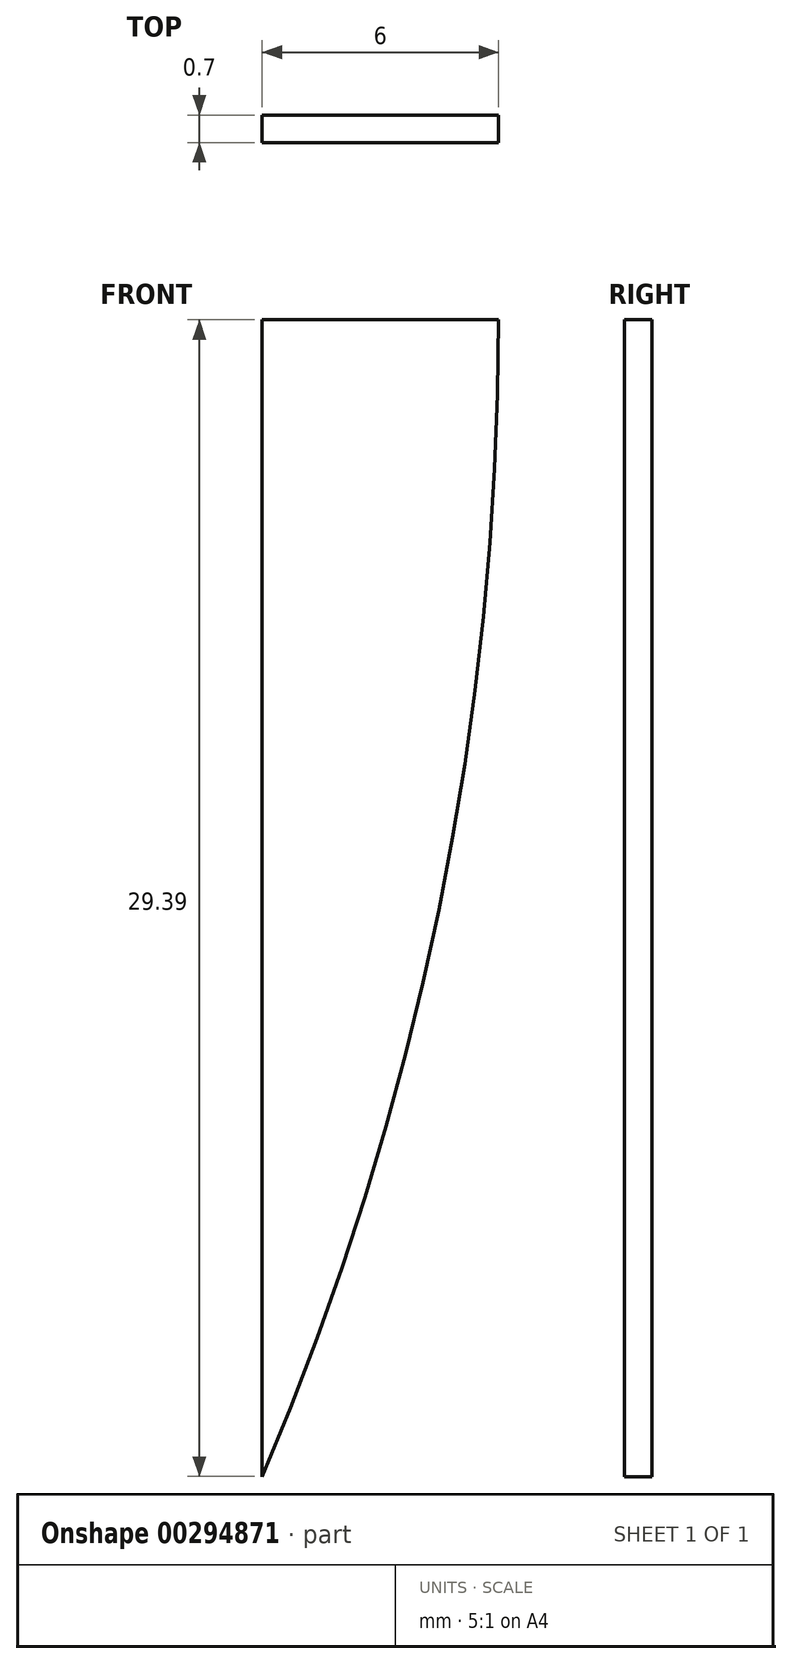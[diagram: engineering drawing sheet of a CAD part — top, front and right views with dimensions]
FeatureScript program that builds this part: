
annotation { "Feature Type Name" : "Feature", "Feature Type Description" : "" }
export const myFeature = defineFeature(function(context is Context, id is Id, definition is map)
    precondition{}
    {
        {
            var Q0;
            Q0=qCreatedBy(makeId("Front.planeOp"),FACE);
            var sketch = newSketch(context, id + "F0", { "sketchPlane" : qUnion([Q0])});
            skCircle(sketch, "E0", {"center": v(0, 0) * mm, "radius": 75 * mm});
            skLineSegment(sketch, "E1", {"start": v(69, 29.4) * mm, "end": v(69, -29.4) * mm});
            skLineSegment(sketch, "E2", {"start": v(75, 0) * mm, "end": v(69, 0) * mm});
            skSolve(sketch);
        }
        {
            var Q0;
            {var subQ0=sQuery(id+"F0.wireOp",EDGE,"E1");var subQ1=sQuery(id+"F0.wireOp",EDGE,"E0");var subQ2=makeQuery(id+"F0.imprint","INTERSECT",VERTEX,{"disambiguationData":[OD(0.0)],"derivedFrom":[subQ1,subQ0]});Q0=makeQuery(id+"F0.imprint","IMPRINT",FACE,{"disambiguationData":[TD([[makeQuery(id+"F0.imprint","IMPRINT",EDGE,{"disambiguationData":[TD([[subQ2,-1.0]])],"derivedFrom":subQ1}),1.0]])]});}
            extrude(context, id + "F1", {"entities" : qUnion([Q0]), "endBound" : BoundingType.SYMMETRIC, "depth" : 0.7 * mm});
        }
    });
